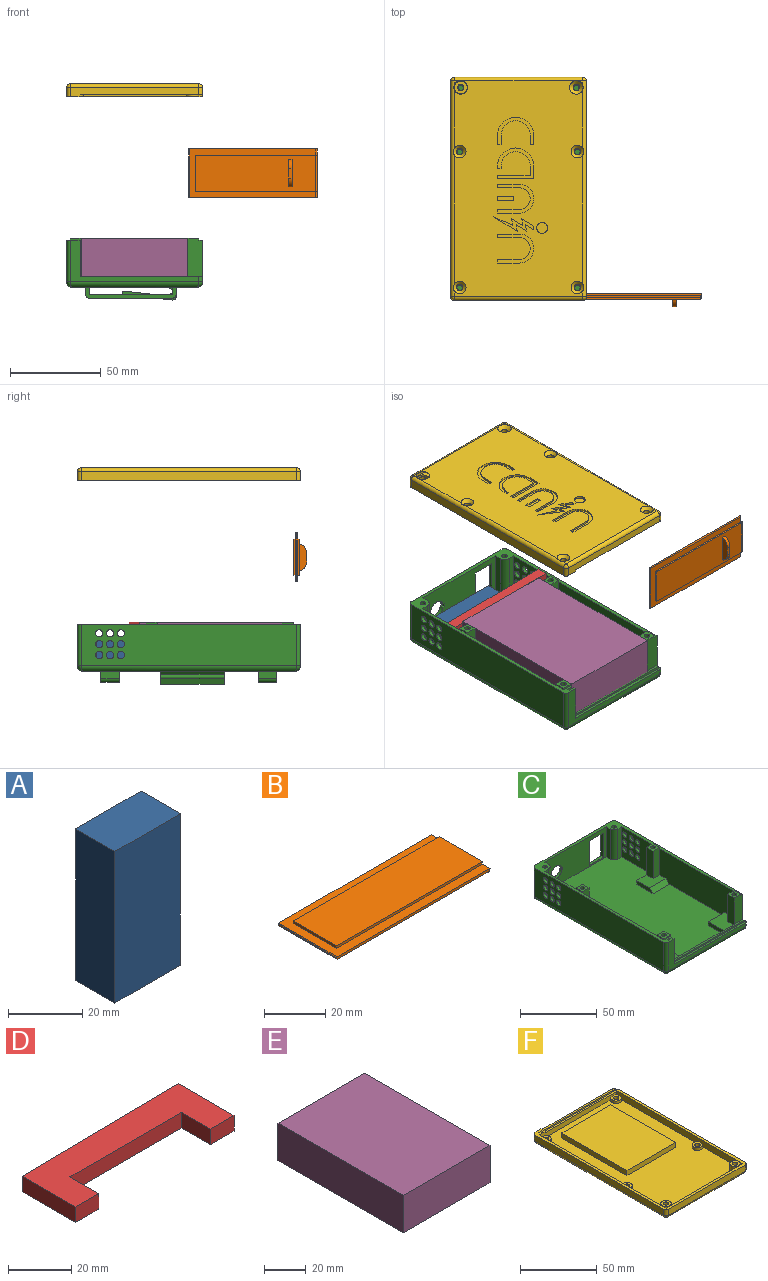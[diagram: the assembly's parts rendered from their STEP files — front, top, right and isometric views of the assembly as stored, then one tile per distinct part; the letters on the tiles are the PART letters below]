
ASSEMBLY  parts=6 mates=9
PART A: 6 faces, bbox 25x15x50 mm
  f0: plane 50x25mm, normal (0,1,0), area 1250mm2, adj f1,f3,f4,f5
  f1: plane 50x15mm, normal (-1,0,0), area 750mm2, adj f0,f2,f4,f5
  f2: plane 50x25mm, normal (0,-1,0), area 1250mm2, adj f1,f3,f4,f5
  f3: plane 50x15mm, normal (1,0,0), area 750mm2, adj f0,f2,f4,f5
  f4: plane 25x15mm, normal (0,0,1), area 375mm2, adj f0,f1,f2,f3
  f5: plane 25x15mm, normal (0,0,-1), area 375mm2, adj f0,f1,f2,f3
PART B: 24 faces, bbox 71x27x7 mm
  f0: plane 66.5x20mm, normal (0,0,-1), area 1300mm2, adj f2,f3,f4,f16,f17,f18,f20,f21
  f1: plane 70.7x27mm, normal (0,0,1), area 558.9mm2, adj f6,f8,f10,f11,f12,f14,f15,f23
  f2: plane 67.5x2mm, normal (0,1,0), area 67.5mm2, adj f0,f3,f5,f9,f15,f16
  f3: plane 20x1mm, normal (-1,0,0), area 20mm2, adj f0,f2,f4,f9
  f4: plane 67.5x2mm, normal (0,-1,0), area 67.5mm2, adj f0,f3,f5,f9,f14,f16
  f5: plane 20x2mm, normal (1,0,0), area 40mm2, adj f2,f4,f11,f12,f13,f16
  f6: plane 71x1mm, normal (0,1,0), area 70.7mm2, adj f1,f7,f9,f15,f22,f23
  f7: plane 27x0.4mm, normal (-1,0,0), area 10.8mm2, adj f6,f8,f22,f23
  f8: plane 71x1mm, normal (0,-1,0), area 70.7mm2, adj f1,f7,f9,f14,f22,f23
  f9: plane 69.7x27mm, normal (0,0,-1), area 551.9mm2, adj f2,f3,f4,f6,f8,f14,f15,f22
  f10: plane 20x1mm, normal (-1,0,0), area 20mm2, adj f1,f11,f12,f13
  f11: plane 67.5x1mm, normal (0,-1,0), area 67.5mm2, adj f1,f5,f10,f13
  f12: plane 67.5x1mm, normal (0,1,0), area 67.5mm2, adj f1,f5,f10,f13
  f13: plane 67.5x20mm, normal (0,0,1), area 1350mm2, adj f5,f10,f11,f12
  f14: cylinder r=1mm len=3.5mm, axis (0,1,0), area 5.5mm2, adj f1,f4,f8,f9
  f15: cylinder r=1mm len=3.5mm, axis (0,1,0), area 5.5mm2, adj f1,f2,f6,f9
  f16: cylinder r=1mm len=20mm, axis (0,1,0), area 31.4mm2, adj f0,f2,f4,f5
  f17: plane 15x4mm, normal (-1,0,0), area 50.1mm2, adj f0,f19,f20,f21
  f18: plane 15x4mm, normal (1,0,0), area 50.1mm2, adj f0,f19,f20,f21
  f19: plane 5.2x2mm, normal (0,0,-1), area 10.4mm2, adj f17,f18,f20,f21
  f20: cylinder r=5mm len=4.9mm, axis (-1,0,0), area 13.7mm2, adj f0,f17,f18,f19
  f21: cylinder r=5mm len=4.9mm, axis (-1,0,0), area 13.7mm2, adj f0,f17,f18,f19
  f22: plane 27x0.3mm, normal (-0.71,0,-0.71), area 11.5mm2, adj f6,f7,f8,f9
  f23: plane 27x0.3mm, normal (-0.71,0,0.71), area 11.5mm2, adj f1,f6,f7,f8
PART C: 143 faces, bbox 75x123x34 mm
  f0: plane 117x69mm, normal (0,0,-1), area 7818mm2, adj f8,f52,f53,f54,f74,f75,f76,f77
  f1: plane 35x1.5mm, normal (-1,0,0), area 52.5mm2, adj f139,f140,f141,f142
  f2: plane 70.97x1.27mm, normal (0,0,1), area 87.9mm2, adj f3,f8,f59,f129,f130,f135,f136,f137
  f3: plane 23.5x1mm, normal (1,0,0), area 23.5mm2, adj f2,f6,f135,f136
  f4: plane 59x4mm, normal (0,1,0), area 182mm2, adj f9,f24,f28,f44,f46,f47,f49,f133
  f5: plane 118.25x23mm, normal (1,0,0), area 2581.7mm2, adj f6,f8,f10,f60,f107,f108,f109,f110
  f6: plane 123x75mm, normal (0,0,1), area 723.3mm2, adj f3,f5,f10,f11,f12,f13,f14,f15
  f7: cylinder r=2mm len=3mm, axis (0,0,1), area 7.9mm2, adj f20,f59,f130,f131
  f8: cylinder r=3mm len=118.99mm, axis (0,1,0), area 555.9mm2, adj f0,f2,f5,f59,f61,f129
  f9: plane 117x71mm, normal (0,0,1), area 7311.4mm2, adj f4,f11,f12,f13,f15,f16,f17,f18
  f10: plane 21x8mm, normal (0,-1,0), area 166mm2, adj f5,f6,f26,f28,f29,f133
  f11: plane 56.8x24mm, normal (0,-1,0), area 1032.9mm2, adj f6,f9,f99,f100,f101,f102,f103,f104
  f12: cylinder r=3.5mm len=24mm, axis (0,0,-1), area 131.9mm2, adj f6,f9,f127,f128
  f13: cylinder r=3.5mm len=24mm, axis (0,0,-1), area 131.9mm2, adj f6,f9,f125,f126
  f14: plane 71x23mm, normal (0,1,0), area 1302.7mm2, adj f6,f52,f55,f60,f99,f101,f102,f103
  f15: plane 28.9x24mm, normal (1,0,0), area 580.5mm2, adj f6,f9,f33,f116,f117,f118,f119,f120
  f16: plane 69x24mm, normal (-1,0,0), area 1606.5mm2, adj f6,f9,f27,f36,f43,f47,f48,f51
  f17: plane 69x24mm, normal (1,0,0), area 1606.5mm2, adj f6,f9,f22,f31,f40,f45,f46,f50
  f18: plane 28.9x24mm, normal (-1,0,0), area 580.5mm2, adj f6,f9,f37,f107,f108,f109,f110,f111
  f19: plane 119x23mm, normal (-1,0,0), area 2623.9mm2, adj f6,f53,f55,f57,f116,f117,f118,f119
  f20: plane 71x23mm, normal (0,-1,0), area 323mm2, adj f6,f7,f54,f57,f131,f132
  f21: plane 6x1mm, normal (-1,0,0), area 6mm2, adj f6,f22,f23,f25
  f22: plane 22x6mm, normal (0,1,0), area 132mm2, adj f17,f21,f24,f25,f46
  f23: plane 21x6mm, normal (0,-1,0), area 16mm2, adj f6,f21,f24,f25,f133,f134
  f24: plane 22x6mm, normal (1,0,0), area 132mm2, adj f4,f22,f23,f25,f46
  f25: plane 6x6mm, normal (0,0,1), area 28.9mm2, adj f21,f22,f23,f24,f68
  f26: plane 6x1mm, normal (1,0,0), area 6mm2, adj f6,f10,f27,f29
  f27: plane 22x6mm, normal (0,1,0), area 132mm2, adj f16,f26,f28,f29,f47
  f28: plane 22x6mm, normal (-1,0,0), area 132mm2, adj f4,f10,f27,f29,f47
  f29: plane 6x6mm, normal (0,0,1), area 28.9mm2, adj f10,f26,f27,f28,f66
  f30: plane 6x1mm, normal (-1,0,0), area 6mm2, adj f6,f31,f33,f34
  f31: plane 22x6mm, normal (0,-1,0), area 132mm2, adj f17,f30,f32,f34,f40
  f32: plane 22x6mm, normal (1,0,0), area 132mm2, adj f31,f33,f34,f40
  f33: plane 25x15mm, normal (0,1,0), area 177mm2, adj f9,f15,f30,f32,f34,f40,f41
  f34: plane 6x6mm, normal (0,0,1), area 28.9mm2, adj f30,f31,f32,f33,f64
  f35: plane 6x1mm, normal (1,0,0), area 6mm2, adj f6,f36,f37,f39
  f36: plane 22x6mm, normal (0,-1,0), area 132mm2, adj f16,f35,f38,f39,f43
  f37: plane 25x15mm, normal (0,1,0), area 177mm2, adj f9,f18,f35,f38,f39,f42,f43
  f38: plane 22x6mm, normal (-1,0,0), area 132mm2, adj f36,f37,f39,f43
  f39: plane 6x6mm, normal (0,0,1), area 28.9mm2, adj f35,f36,f37,f38,f62
  f40: plane 15x12mm, normal (0,0,1), area 144mm2, adj f17,f31,f32,f33,f41,f50
  f41: plane 15x3mm, normal (1,0,0), area 40.5mm2, adj f9,f33,f40,f50
  f42: plane 15x3mm, normal (-1,0,0), area 40.5mm2, adj f9,f37,f43,f51
  f43: plane 15x12mm, normal (0,0,1), area 144mm2, adj f16,f36,f37,f38,f42,f51
  f44: plane 15x3mm, normal (1,0,0), area 45mm2, adj f4,f9,f45,f46
  f45: plane 15x3mm, normal (0,1,0), area 45mm2, adj f9,f17,f44,f46
  f46: plane 15x15mm, normal (0,0,1), area 189mm2, adj f4,f17,f22,f24,f44,f45
  f47: plane 15x15mm, normal (0,0,1), area 189mm2, adj f4,f16,f27,f28,f48,f49
  f48: plane 15x3mm, normal (0,1,0), area 45mm2, adj f9,f16,f47,f49
  f49: plane 15x3mm, normal (-1,0,0), area 45mm2, adj f4,f9,f47,f48
  f50: plane 15x3mm, normal (0,-0.71,0.71), area 63.6mm2, adj f9,f17,f40,f41
  f51: plane 15x3mm, normal (0,-0.71,0.71), area 63.6mm2, adj f9,f16,f42,f43
  f52: cylinder r=3mm len=71mm, axis (-1,0,0), area 329.9mm2, adj f0,f14,f56,f61,f100
  f53: cylinder r=3mm len=119mm, axis (0,-1,0), area 556.1mm2, adj f0,f19,f56,f58
  f54: cylinder r=3mm len=71mm, axis (1,0,0), area 329.9mm2, adj f0,f20,f58,f59
  f55: cylinder r=2mm len=23mm, axis (0,0,1), area 72.3mm2, adj f6,f14,f19,f56
  f56: bspline ~3.65x3mm, area 6.6mm2, adj f52,f53,f55
  f57: cylinder r=2mm len=23mm, axis (0,0,-1), area 72.3mm2, adj f6,f19,f20,f58
  f58: bspline ~3.65x3mm, area 6.6mm2, adj f53,f54,f57
  f59: bspline ~3.16x3mm, area 9.5mm2, adj f2,f7,f8,f54,f130
  f60: cylinder r=2mm len=23mm, axis (0,0,-1), area 72.3mm2, adj f5,f6,f14,f61
  f61: bspline ~3.16x3mm, area 6.6mm2, adj f8,f52,f60
  f62: cylinder r=1.5mm len=15mm, axis (0,0,1), area 141.4mm2, adj f39,f63
  f63: plane 3x3mm, normal (0,0,1), area 7.1mm2, adj f62
  f64: cylinder r=1.5mm len=15mm, axis (0,0,1), area 141.4mm2, adj f34,f65
  f65: plane 3x3mm, normal (0,0,1), area 7.1mm2, adj f64
  f66: cylinder r=1.5mm len=15mm, axis (0,0,1), area 141.4mm2, adj f29,f67
  f67: plane 3x3mm, normal (0,0,1), area 7.1mm2, adj f66
  f68: cylinder r=1.5mm len=15mm, axis (0,0,1), area 141.4mm2, adj f25,f69
  f69: plane 3x3mm, normal (0,0,1), area 7.1mm2, adj f68
  f70: cylinder r=1.5mm len=10mm, axis (0,0,1), area 94.2mm2, adj f6,f71
  f71: plane 3x3mm, normal (0,0,1), area 7.1mm2, adj f70
  f72: cylinder r=1.5mm len=10mm, axis (0,0,1), area 94.2mm2, adj f6,f73
  f73: plane 3x3mm, normal (0,0,1), area 7.1mm2, adj f72
  f74: plane 10x4mm, normal (-1,0,0), area 40mm2, adj f0,f75,f77,f93
  f75: plane 50x6mm, normal (0,1,0), area 114.3mm2, adj f0,f74,f76,f78,f87,f88,f89,f92
  f76: plane 10x4mm, normal (1,0,0), area 40mm2, adj f0,f75,f77,f92
  f77: plane 50x6mm, normal (0,-1,0), area 114.3mm2, adj f0,f74,f76,f78,f87,f88,f89,f92
  f78: plane 46x10mm, normal (0,0,-1), area 460mm2, adj f75,f77,f92,f93
  f79: plane 10x4mm, normal (-1,0,0), area 40mm2, adj f0,f80,f82,f91
  f80: plane 50x6mm, normal (0,1,0), area 114.3mm2, adj f0,f79,f81,f83,f84,f85,f86,f90
  f81: plane 10x4mm, normal (1,0,0), area 40mm2, adj f0,f80,f82,f90
  f82: plane 50x6mm, normal (0,-1,0), area 114.3mm2, adj f0,f79,f81,f83,f84,f85,f86,f90
  f83: plane 46x10mm, normal (0,0,-1), area 460mm2, adj f80,f82,f90,f91
  f84: plane 10x4mm, normal (1,0,0), area 40mm2, adj f0,f80,f82,f85
  f85: plane 46x10mm, normal (0,0,1), area 460mm2, adj f80,f82,f84,f86
  f86: plane 10x4mm, normal (-1,0,0), area 40mm2, adj f0,f80,f82,f85
  f87: plane 10x4mm, normal (-1,0,0), area 40mm2, adj f0,f75,f77,f88
  f88: plane 46x10mm, normal (0,0,1), area 460mm2, adj f75,f77,f87,f89
  f89: plane 10x4mm, normal (1,0,0), area 40mm2, adj f0,f75,f77,f88
  f90: cylinder r=2mm len=10mm, axis (0,1,0), area 31.4mm2, adj f80,f81,f82,f83
  f91: cylinder r=2mm len=10mm, axis (0,-1,0), area 31.4mm2, adj f79,f80,f82,f83
  f92: cylinder r=2mm len=10mm, axis (0,1,0), area 31.4mm2, adj f75,f76,f77,f78
  f93: cylinder r=2mm len=10mm, axis (0,-1,0), area 31.4mm2, adj f74,f75,f77,f78
  f94: plane 35x5mm, normal (1,0,0), area 175mm2, adj f0,f97,f141,f142
  f95: plane 35x26.61mm, normal (-0.11,0,-0.99), area 937mm2, adj f97,f98,f141,f142
  f96: plane 35x23.63mm, normal (0.11,0,0.99), area 832mm2, adj f98,f140,f141,f142
  f97: cylinder r=2mm len=35mm, axis (0,-1,0), area 117.5mm2, adj f94,f95,f141,f142
  f98: cylinder r=1mm len=35mm, axis (0,1,0), area 110mm2, adj f95,f96,f141,f142
  f99: plane 19.4x2mm, normal (-1,0,0), area 38.8mm2, adj f11,f14,f100,f102
  f100: plane 12.9x2mm, normal (0,0,1), area 25.8mm2, adj f11,f52,f99,f101
  f101: plane 19.4x2mm, normal (1,0,0), area 38.8mm2, adj f11,f14,f100,f102
  f102: plane 12.9x2mm, normal (0,0,-1), area 25.8mm2, adj f11,f14,f99,f101
  f103: plane 2x0.96mm, normal (0,0,1), area 1.9mm2, adj f11,f14,f104,f106
  f104: cylinder r=5mm len=10mm, axis (0,1,0), area 59.6mm2, adj f11,f14,f103,f105
  f105: plane 2x0.96mm, normal (0,0,-1), area 1.9mm2, adj f11,f14,f104,f106
  f106: plane 2x1.6mm, normal (-1,0,0), area 3.2mm2, adj f11,f14,f103,f105
  f107: cylinder r=2mm len=4mm, axis (1,0,0), area 25.1mm2, adj f5,f18
  f108: cylinder r=2mm len=4mm, axis (1,0,0), area 25.1mm2, adj f5,f18
  f109: cylinder r=2mm len=4mm, axis (1,0,0), area 25.1mm2, adj f5,f18
  f110: cylinder r=2mm len=4mm, axis (1,0,0), area 25.1mm2, adj f5,f18
  f111: cylinder r=2mm len=4mm, axis (1,0,0), area 25.1mm2, adj f5,f18
  f112: cylinder r=2mm len=4mm, axis (1,0,0), area 25.1mm2, adj f5,f18
  f113: cylinder r=2mm len=4mm, axis (1,0,0), area 25.1mm2, adj f5,f18
  f114: cylinder r=2mm len=4mm, axis (1,0,0), area 25.1mm2, adj f5,f18
  f115: cylinder r=2mm len=4mm, axis (1,0,0), area 25.1mm2, adj f5,f18
  f116: cylinder r=2mm len=4mm, axis (1,0,0), area 25.1mm2, adj f15,f19
  f117: cylinder r=2mm len=4mm, axis (1,0,0), area 25.1mm2, adj f15,f19
  f118: cylinder r=2mm len=4mm, axis (1,0,0), area 25.1mm2, adj f15,f19
  f119: cylinder r=2mm len=4mm, axis (1,0,0), area 25.1mm2, adj f15,f19
  f120: cylinder r=2mm len=4mm, axis (1,0,0), area 25.1mm2, adj f15,f19
  f121: cylinder r=2mm len=4mm, axis (1,0,0), area 25.1mm2, adj f15,f19
  f122: cylinder r=2mm len=4mm, axis (1,0,0), area 25.1mm2, adj f15,f19
  f123: cylinder r=2mm len=4mm, axis (1,0,0), area 25.1mm2, adj f15,f19
  f124: cylinder r=2mm len=4mm, axis (1,0,0), area 25.1mm2, adj f15,f19
  f125: plane 24x3.6mm, normal (1,0,0), area 86.4mm2, adj f6,f9,f11,f13
  f126: plane 24x3.6mm, normal (0,-1,0), area 86.4mm2, adj f6,f9,f13,f15
  f127: plane 24x3.6mm, normal (0,-1,0), area 86.4mm2, adj f6,f9,f12,f18
  f128: plane 24x3.6mm, normal (-1,0,0), area 86.4mm2, adj f6,f9,f11,f12
  f129: plane 67.63x3.5mm, normal (0,-1,0), area 236.7mm2, adj f2,f5,f8,f133,f137
  f130: plane 67.57x3.51mm, normal (0,1,0), area 236.5mm2, adj f2,f7,f59,f131,f138
  f131: plane 67.56x1.5mm, normal (0,0,1), area 100.4mm2, adj f7,f20,f130,f132,f138
  f132: plane 20x1.38mm, normal (1,0,0), area 27.5mm2, adj f6,f20,f131,f138
  f133: plane 67.63x1.25mm, normal (0,0,1), area 84.4mm2, adj f4,f5,f10,f23,f129,f134,f137
  f134: plane 20x1.13mm, normal (1,0,0), area 22.5mm2, adj f6,f23,f133,f137
  f135: plane 23.5x3.25mm, normal (0,1,0), area 76.4mm2, adj f2,f3,f6,f138
  f136: plane 23.5x3.25mm, normal (0,-1,0), area 76.4mm2, adj f2,f3,f6,f137
  f137: plane 23.5x0.25mm, normal (0.71,-0.71,0), area 7.7mm2, adj f2,f6,f129,f133,f134,f136
  f138: plane 23.5x0.25mm, normal (0.71,0.71,0), area 7.7mm2, adj f2,f6,f130,f131,f132,f135
  f139: plane 35x3mm, normal (-0.45,0,-0.89), area 117.4mm2, adj f0,f1,f141,f142
  f140: plane 35x2.98mm, normal (-0.49,0,0.87), area 119.7mm2, adj f1,f96,f141,f142
  f141: plane 29.72x7mm, normal (0,-1,0), area 73.7mm2, adj f0,f1,f94,f95,f96,f97,f98,f139
  f142: plane 29.72x7mm, normal (0,1,0), area 73.7mm2, adj f0,f1,f94,f95,f96,f97,f98,f139
PART D: 10 faces, bbox 71x25x6 mm
  f0: plane 10.5x6mm, normal (0,-1,0), area 63mm2, adj f1,f7,f8,f9
  f1: plane 25x6mm, normal (1,0,0), area 150mm2, adj f0,f2,f8,f9
  f2: plane 71x6mm, normal (-0.01,1,0), area 426mm2, adj f1,f3,f8,f9
  f3: plane 24x6mm, normal (-1,0,0), area 144mm2, adj f2,f4,f8,f9
  f4: plane 10.5x6mm, normal (0,-1,0), area 63mm2, adj f3,f5,f8,f9
  f5: plane 13x6mm, normal (1,0,0), area 78mm2, adj f4,f6,f8,f9
  f6: plane 50x6mm, normal (0,-1,0), area 300mm2, adj f5,f7,f8,f9
  f7: plane 13x6mm, normal (-1,0,0), area 78mm2, adj f0,f6,f8,f9
  f8: plane 71x25mm, normal (0,0,1), area 1089.5mm2, adj f0,f1,f2,f3,f4,f5,f6,f7
  f9: plane 71x25mm, normal (0,0,-1), area 1089.5mm2, adj f0,f1,f2,f3,f4,f5,f6,f7
PART E: 6 faces, bbox 59x85x22 mm
  f0: plane 59x22mm, normal (0,1,0), area 1298mm2, adj f1,f3,f4,f5
  f1: plane 85x22mm, normal (-1,0,0), area 1870mm2, adj f0,f2,f4,f5
  f2: plane 59x22mm, normal (0,-1,0), area 1298mm2, adj f1,f3,f4,f5
  f3: plane 85x22mm, normal (1,0,0), area 1870mm2, adj f0,f2,f4,f5
  f4: plane 85x59mm, normal (0,0,1), area 5015mm2, adj f0,f1,f2,f3
  f5: plane 85x59mm, normal (0,0,-1), area 5015mm2, adj f0,f1,f2,f3
PART F: 128 faces, bbox 75x123x7 mm
  f0: plane 3.5x1mm, normal (1,0,0), area 3.5mm2, adj f1,f5,f124,f125
  f1: plane 71x1.25mm, normal (0,0,1), area 87.9mm2, adj f0,f6,f7,f8,f9,f124,f125,f126
  f2: plane 67.5x1.25mm, normal (0,0,1), area 84.4mm2, adj f7,f9,f120,f121,f123
  f3: plane 67.44x1.5mm, normal (0,0,1), area 100.4mm2, adj f4,f6,f8,f122
  f4: plane 71x5mm, normal (0,1,0), area 289.5mm2, adj f3,f5,f6,f30,f31,f122
  f5: plane 123x75mm, normal (0,0,1), area 641.9mm2, adj f0,f4,f9,f10,f11,f23,f24,f26
  f6: cylinder r=2mm len=4mm, axis (0,0,1), area 11.3mm2, adj f1,f3,f4,f8,f9,f27
  f7: plane 67.5x2.5mm, normal (0,1,0), area 168.8mm2, adj f1,f2,f9,f126
  f8: plane 67.44x2.5mm, normal (0,-1,0), area 168.6mm2, adj f1,f3,f6,f127
  f9: plane 119x5mm, normal (1,0,0), area 591.1mm2, adj f1,f2,f5,f6,f7,f28,f29,f121
  f10: plane 117x5mm, normal (-1,0,0), area 570.6mm2, adj f5,f13,f17,f18,f19,f21,f26,f57
  f11: plane 117x5mm, normal (1,0,0), area 570.6mm2, adj f5,f12,f13,f14,f15,f16,f26,f55
  f12: plane 1.2x1.2mm, normal (0,0,1), area 0.6mm2, adj f11,f15,f120
  f13: plane 117x71mm, normal (0,0,1), area 5382.2mm2, adj f10,f11,f14,f18,f26,f38,f39,f40
  f14: cylinder r=3.5mm len=6.5mm, axis (0,0,-1), area 25.4mm2, adj f11,f13,f16,f120
  f15: cylinder r=3.5mm len=2mm, axis (0,0,-1), area 3.4mm2, adj f11,f12,f16,f120
  f16: plane 6.5x6.5mm, normal (0,0,1), area 26.4mm2, adj f11,f14,f15,f62,f120
  f17: cylinder r=3.5mm len=2mm, axis (0,0,-1), area 3.4mm2, adj f10,f19,f21,f120
  f18: cylinder r=3.5mm len=6.5mm, axis (0,0,-1), area 25.4mm2, adj f10,f13,f19,f120
  f19: plane 6.5x6.5mm, normal (0,0,1), area 26.4mm2, adj f10,f17,f18,f61,f120
  f20: plane 119x71mm, normal (0,0,-1), area 7740.5mm2, adj f29,f30,f34,f35,f49,f50,f51,f52
  f21: plane 1.2x1.2mm, normal (0,0,1), area 0.6mm2, adj f10,f17,f120
  f22: plane 2.55x2.55mm, normal (0,0,-1), area 2.1mm2, adj f29,f34,f54
  f23: plane 119x5mm, normal (-1,0,0), area 595mm2, adj f5,f31,f35,f37
  f24: plane 71x5mm, normal (0,-1,0), area 355mm2, adj f5,f28,f34,f37
  f25: plane 2.55x2.55mm, normal (0,0,-1), area 2.1mm2, adj f34,f35,f53
  f26: plane 71x5mm, normal (0,1,0), area 355mm2, adj f5,f10,f11,f13
  f27: sphere r=2mm, area 6.3mm2, adj f6,f29,f30
  f28: cylinder r=2mm len=5mm, axis (0,0,-1), area 15.7mm2, adj f5,f9,f24,f32
  f29: cylinder r=2mm len=119mm, axis (0,1,0), area 371.4mm2, adj f9,f20,f22,f27,f32,f50,f51,f54
  f30: cylinder r=2mm len=71mm, axis (-1,0,0), area 223.1mm2, adj f4,f20,f27,f33
  f31: cylinder r=2mm len=5mm, axis (0,0,-1), area 15.7mm2, adj f4,f5,f23,f33
  f32: sphere r=2mm, area 6.3mm2, adj f28,f29,f34
  f33: sphere r=2mm, area 6.3mm2, adj f30,f31,f35
  f34: cylinder r=2mm len=71mm, axis (1,0,0), area 222.6mm2, adj f20,f22,f24,f25,f32,f36,f53,f54
  f35: cylinder r=2mm len=119mm, axis (0,-1,0), area 371.4mm2, adj f20,f23,f25,f33,f36,f49,f52,f53
  f36: sphere r=2mm, area 6.3mm2, adj f34,f35,f37
  f37: cylinder r=2mm len=5mm, axis (0,0,1), area 15.7mm2, adj f5,f23,f24,f36
  f38: plane 60x4mm, normal (-1,0,0), area 240mm2, adj f13,f39,f41,f42
  f39: plane 45x4mm, normal (0,-1,0), area 180mm2, adj f13,f38,f40,f42
  f40: plane 60x4mm, normal (1,0,0), area 240mm2, adj f13,f39,f41,f42
  f41: plane 45x4mm, normal (0,1,0), area 180mm2, adj f13,f38,f40,f42
  f42: plane 60x45mm, normal (0,0,1), area 2700mm2, adj f38,f39,f40,f41
  f43: cylinder r=3.5mm len=7mm, axis (0,0,-1), area 110mm2, adj f13,f44
  f44: plane 7x7mm, normal (0,0,1), area 28.9mm2, adj f43,f48
  f45: cylinder r=3.5mm len=7mm, axis (0,0,-1), area 110mm2, adj f13,f46
  f46: plane 7x7mm, normal (0,0,1), area 28.9mm2, adj f45,f47
  f47: cylinder r=1.75mm len=5mm, axis (0,0,1), area 55mm2, adj f46,f54
  f48: cylinder r=1.75mm len=5mm, axis (0,0,1), area 55mm2, adj f44,f53
  f49: cone r=3.5mm half-angle=45deg, axis (0,0,-1), area 40.7mm2, adj f20,f35,f62
  f50: cone r=3.5mm half-angle=45deg, axis (0,0,-1), area 40.7mm2, adj f20,f29,f61
  f51: cone r=3.5mm half-angle=45deg, axis (0,0,-1), area 40.7mm2, adj f20,f29,f59
  f52: cone r=3.5mm half-angle=45deg, axis (0,0,-1), area 40.7mm2, adj f20,f35,f60
  f53: cone r=3.75mm half-angle=45deg, axis (0,0,-1), area 48.9mm2, adj f20,f25,f34,f35,f48
  f54: cone r=3.75mm half-angle=45deg, axis (0,0,-1), area 48.9mm2, adj f20,f22,f29,f34,f47
  f55: cylinder r=3.5mm len=7mm, axis (0,0,-1), area 36.4mm2, adj f11,f13,f56
  f56: plane 7x6.5mm, normal (0,0,1), area 27.6mm2, adj f11,f55,f60
  f57: cylinder r=3.5mm len=7mm, axis (0,0,-1), area 36.4mm2, adj f10,f13,f58
  f58: plane 7x6.5mm, normal (0,0,1), area 27.6mm2, adj f10,f57,f59
  f59: cylinder r=1.75mm len=3.5mm, axis (0,0,-1), area 24.7mm2, adj f51,f58
  f60: cylinder r=1.75mm len=3.5mm, axis (0,0,-1), area 24.7mm2, adj f52,f56
  f61: cylinder r=1.75mm len=3.5mm, axis (0,0,-1), area 24.7mm2, adj f19,f50
  f62: cylinder r=1.75mm len=3.5mm, axis (0,0,-1), area 24.7mm2, adj f16,f49
  f63: plane 13.01x8.06mm, normal (0.53,-0.85,0), area 15.3mm2, adj f20,f64,f73,f74
  f64: plane 3.68x1mm, normal (-0.99,0.14,0), area 3.7mm2, adj f20,f63,f65,f74
  f65: plane 5.58x3.46mm, normal (0.53,-0.85,0), area 6.6mm2, adj f20,f64,f66,f74
  f66: plane 3.56x1mm, normal (-0.99,0.14,0), area 3.6mm2, adj f20,f65,f67,f74
  f67: plane 4.56x2.83mm, normal (0.53,-0.85,0), area 5.4mm2, adj f20,f66,f68,f74
  f68: plane 2x1mm, normal (-1,0,0), area 2mm2, adj f20,f67,f69,f74
  f69: plane 6.63x4.11mm, normal (-0.53,0.85,0), area 7.8mm2, adj f20,f68,f70,f74
  f70: plane 3.82x1mm, normal (0.99,-0.14,0), area 3.9mm2, adj f20,f69,f71,f74
  f71: plane 6.16x3.82mm, normal (-0.53,0.85,0), area 7.2mm2, adj f20,f70,f72,f74
  f72: plane 3.66x1mm, normal (0.99,-0.14,0), area 3.7mm2, adj f20,f71,f73,f74
  f73: plane 10.4x4.66mm, normal (-0.41,0.91,0), area 11.4mm2, adj f20,f63,f72,f74
  f74: plane 22.11x8.06mm, normal (0,0,-1), area 46.9mm2, adj f63,f64,f65,f66,f67,f68,f69,f70
  f75: plane 2.5x1mm, normal (1,0,0), area 2.5mm2, adj f20,f76,f78,f79
  f76: plane 9x1mm, normal (0,-1,0), area 9mm2, adj f20,f75,f77,f79
  f77: plane 2.5x1mm, normal (-1,0,0), area 2.5mm2, adj f20,f76,f78,f79
  f78: plane 9x1mm, normal (0,1,0), area 9mm2, adj f20,f75,f77,f79
  f79: plane 9x2.5mm, normal (0,0,-1), area 22.5mm2, adj f75,f76,f77,f78
  f80: plane 12x1mm, normal (0,1,0), area 12mm2, adj f20,f81,f87,f88
  f81: plane 2x1mm, normal (1,0,0), area 2mm2, adj f20,f80,f82,f88
  f82: plane 12x1mm, normal (0,-1,0), area 12mm2, adj f20,f81,f83,f88
  f83: cylinder r=8mm len=16mm, axis (0,0,-1), area 25.1mm2, adj f20,f82,f84,f88
  f84: plane 12x1mm, normal (0,1,0), area 12mm2, adj f20,f83,f85,f88
  f85: plane 2x1mm, normal (1,0,0), area 2mm2, adj f20,f84,f86,f88
  f86: plane 12x1mm, normal (0,-1,0), area 12mm2, adj f20,f85,f87,f88
  f87: cylinder r=6mm len=12mm, axis (0,0,-1), area 18.8mm2, adj f20,f80,f86,f88
  f88: plane 20x16mm, normal (0,0,-1), area 92mm2, adj f80,f81,f82,f83,f84,f85,f86,f87
  f89: plane 2x1mm, normal (0,-1,0), area 2mm2, adj f20,f90,f98,f99
  f90: plane 1.5x1mm, normal (-1,0,0), area 1.5mm2, adj f20,f89,f91,f99
  f91: cylinder r=8mm len=16mm, axis (0,0,-1), area 25.1mm2, adj f20,f90,f92,f99
  f92: plane 5x1mm, normal (1,0,0), area 5mm2, adj f20,f91,f93,f99
  f93: plane 18x1mm, normal (0,1,0), area 18mm2, adj f20,f92,f94,f99
  f94: plane 2x1mm, normal (1,0,0), area 2mm2, adj f20,f93,f95,f99
  f95: plane 20x1mm, normal (0,-1,0), area 20mm2, adj f20,f94,f96,f99
  f96: plane 7x1mm, normal (-1,0,0), area 7mm2, adj f20,f95,f97,f99
  f97: cylinder r=10mm len=20mm, axis (0,0,-1), area 31.4mm2, adj f20,f96,f98,f99
  f98: plane 1.5x1mm, normal (1,0,0), area 1.5mm2, adj f20,f89,f97,f99
  f99: plane 20x17mm, normal (0,0,-1), area 109.5mm2, adj f89,f90,f91,f92,f93,f94,f95,f96
  f100: cylinder r=3mm len=6mm, axis (0,0,-1), area 18.8mm2, adj f20,f101
  f101: plane 6x6mm, normal (0,0,-1), area 28.3mm2, adj f100
  f102: plane 12x1mm, normal (0,1,0), area 12mm2, adj f20,f103,f109,f110
  f103: plane 2x1mm, normal (1,0,0), area 2mm2, adj f20,f102,f104,f110
  f104: plane 12x1mm, normal (0,-1,0), area 12mm2, adj f20,f103,f105,f110
  f105: cylinder r=8mm len=16mm, axis (0,0,-1), area 25.1mm2, adj f20,f104,f106,f110
  f106: plane 12x1mm, normal (0,1,0), area 12mm2, adj f20,f105,f107,f110
  f107: plane 2x1mm, normal (1,0,0), area 2mm2, adj f20,f106,f108,f110
  f108: plane 12x1mm, normal (0,-1,0), area 12mm2, adj f20,f107,f109,f110
  f109: cylinder r=6mm len=12mm, axis (0,0,-1), area 18.8mm2, adj f20,f102,f108,f110
  f110: plane 20x16mm, normal (0,0,-1), area 92mm2, adj f102,f103,f104,f105,f106,f107,f108,f109
  f111: plane 5x1mm, normal (-1,0,0), area 5mm2, adj f20,f112,f118,f119
  f112: cylinder r=10mm len=20mm, axis (0,0,-1), area 31.4mm2, adj f20,f111,f113,f119
  f113: plane 5x1mm, normal (1,0,0), area 5mm2, adj f20,f112,f114,f119
  f114: plane 2x1mm, normal (0,-1,0), area 2mm2, adj f20,f113,f115,f119
  f115: plane 5x1mm, normal (-1,0,0), area 5mm2, adj f20,f114,f116,f119
  f116: cylinder r=8mm len=16mm, axis (0,0,-1), area 25.1mm2, adj f20,f115,f117,f119
  f117: plane 5x1mm, normal (1,0,0), area 5mm2, adj f20,f116,f118,f119
  f118: plane 2x1mm, normal (0,-1,0), area 2mm2, adj f20,f111,f117,f119
  f119: plane 20x15mm, normal (0,0,-1), area 76.5mm2, adj f111,f112,f113,f114,f115,f116,f117,f118
  f120: plane 71x5mm, normal (0,-1,0), area 275.1mm2, adj f2,f5,f10,f11,f12,f13,f14,f15
  f121: plane 2x1mm, normal (0,1,0), area 2mm2, adj f2,f5,f9,f10
  f122: plane 1.5x1mm, normal (1,0,0), area 1.5mm2, adj f3,f4,f5,f127
  f123: plane 1.25x1mm, normal (1,0,0), area 1.3mm2, adj f2,f5,f120,f126
  f124: plane 3.5x3.38mm, normal (0,-1,0), area 11.8mm2, adj f0,f1,f5,f127
  f125: plane 3.5x3.38mm, normal (0,1,0), area 11.8mm2, adj f0,f1,f5,f126
  f126: plane 3.5x0.13mm, normal (0.71,0.71,0), area 0.6mm2, adj f1,f5,f7,f123,f125
  f127: plane 3.5x0.13mm, normal (0.71,-0.71,0), area 0.6mm2, adj f1,f5,f8,f122,f124
PLACE A rot(axis=(0.58,-0.58,-0.58),120deg) t=(-146.11,24.17,178.2)mm
PLACE B rot(axis=(-1,0,0),90deg) t=(-89.6,-42.46,244.05)mm
PLACE C t=(-114.84,-1.54,202.06)mm
PLACE D rot(axis=(1,0,0),90deg) t=(-68.22,51.54,239.52)mm
PLACE E t=(-161.81,1.59,207.06)mm
PLACE F rot(axis=(1,0,0),180deg) t=(-129.5,25.82,314.32)mm
MATE planar E.f1 <-> C.f32  axis (-1,0,0) through (-190.39,3.04,218.06)mm
MATE planar E.f2 <-> B.f13  axis (0,-1,0) through (-160.89,-39.46,218.06)mm
MATE planar B.f9 <-> C.f130  axis (0,-1,0) through (-127.45,-41.46,275)mm
MATE planar E.f5 <-> C.f46  axis (0,0,-1) through (-160.89,3.04,207.06)mm
MATE planar D.f8 <-> E.f0  axis (0,-1,0) through (-125.39,45.54,216.56)mm
MATE planar A.f2 <-> C.f9  axis (0,0,-1) through (-171.11,57.14,204.06)mm
MATE planar D.f4 <-> C.f9  axis (0,0,-1) through (-191.14,48.54,204.06)mm
MATE slider F.f17 <-> C.f66  axis (0,0,1) through (-128.39,-35.96,311.45)mm
MATE planar D.f1 <-> C.f18  axis (1,0,0) through (-125.39,48.54,216.56)mm
